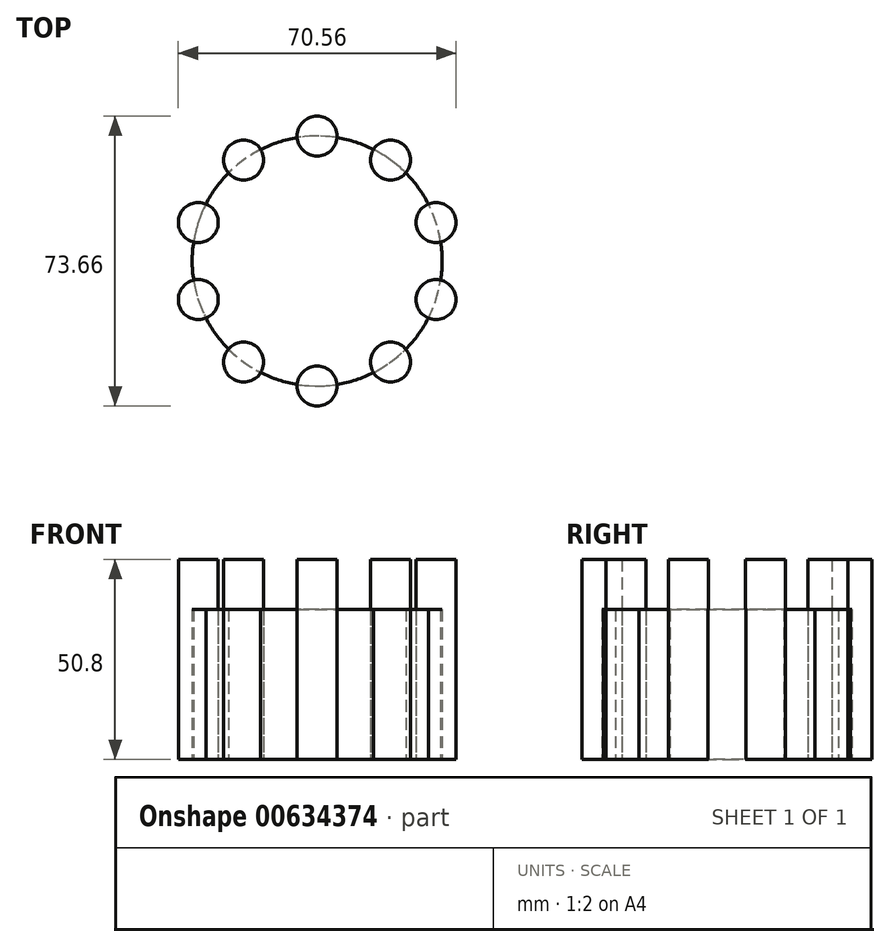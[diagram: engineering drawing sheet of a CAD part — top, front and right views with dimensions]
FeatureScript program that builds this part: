
annotation { "Feature Type Name" : "Feature", "Feature Type Description" : "" }
export const myFeature = defineFeature(function(context is Context, id is Id, definition is map)
    precondition{}
    {
        {
            var Q0;
            Q0=qCreatedBy(makeId("Top.planeOp"),FACE);
            var sketch = newSketch(context, id + "F0", { "sketchPlane" : qUnion([Q0])});
            skCircle(sketch, "E0", {"center": v(0, 0) * mm, "radius": 31.75 * mm});
            skSolve(sketch);
        }
        {
            var Q0;
            Q0=qSketchRegion(id+"F0",true);
            extrude(context, id + "F1", {"entities" : qUnion([Q0]), "depth" : 38.1 * mm});
        }
        {
            var Q0;
            Q0=qCreatedBy(makeId("Top.planeOp"),FACE);
            var sketch = newSketch(context, id + "F2", { "sketchPlane" : qUnion([Q0])});
            skCircle(sketch, "E1", {"center": v(0, 31.75) * mm, "radius": 5.08 * mm});
            skCircle(sketch, "E2.1.0", {"center": v(-18.66, 25.69) * mm, "radius": 5.08 * mm});
            skCircle(sketch, "E2.2.0", {"center": v(-30.2, 9.81) * mm, "radius": 5.08 * mm});
            skCircle(sketch, "E2.3.0", {"center": v(-30.2, -9.81) * mm, "radius": 5.08 * mm});
            skCircle(sketch, "E2.4.0", {"center": v(-18.66, -25.69) * mm, "radius": 5.08 * mm});
            skCircle(sketch, "E2.5.0", {"center": v(0, -31.75) * mm, "radius": 5.08 * mm});
            skCircle(sketch, "E2.6.0", {"center": v(18.66, -25.69) * mm, "radius": 5.08 * mm});
            skCircle(sketch, "E2.7.0", {"center": v(30.2, -9.81) * mm, "radius": 5.08 * mm});
            skCircle(sketch, "E2.8.0", {"center": v(30.2, 9.81) * mm, "radius": 5.08 * mm});
            skCircle(sketch, "E2.9.0", {"center": v(18.66, 25.69) * mm, "radius": 5.08 * mm});
            skPoint(sketch, "E2.center", {"position": v(0, 0) * mm});
            skSolve(sketch);
        }
        {
            var Q0;
            Q0=qSketchRegion(id+"F2",true);
            extrude(context, id + "F3", {"entities" : qUnion([Q0]), "depth" : 50.8 * mm});
        }
        {
            var Q0;
            Q0=makeQuery(id+"F1.opExtrude","SWEPT_BODY",BODY,{"disambiguationData":[OSD([sQuery(id+"F0.wireOp",EDGE,"E0")])]});
            var Q1;
            Q1=makeQuery(id+"F3.opExtrude","SWEPT_BODY",BODY,{"disambiguationData":[OSD([sQuery(id+"F2.wireOp",EDGE,"E1")])]});
            var Q2;
            Q2=makeQuery(id+"F3.opExtrude","SWEPT_BODY",BODY,{"disambiguationData":[OSD([sQuery(id+"F2.wireOp",EDGE,"E2.1.0")])]});
            var Q3;
            Q3=makeQuery(id+"F3.opExtrude","SWEPT_BODY",BODY,{"disambiguationData":[OSD([sQuery(id+"F2.wireOp",EDGE,"E2.2.0")])]});
            var Q4;
            Q4=makeQuery(id+"F3.opExtrude","SWEPT_BODY",BODY,{"disambiguationData":[OSD([sQuery(id+"F2.wireOp",EDGE,"E2.3.0")])]});
            var Q5;
            Q5=makeQuery(id+"F3.opExtrude","SWEPT_BODY",BODY,{"disambiguationData":[OSD([sQuery(id+"F2.wireOp",EDGE,"E2.4.0")])]});
            var Q6;
            Q6=makeQuery(id+"F3.opExtrude","SWEPT_BODY",BODY,{"disambiguationData":[OSD([sQuery(id+"F2.wireOp",EDGE,"E2.5.0")])]});
            var Q7;
            Q7=makeQuery(id+"F3.opExtrude","SWEPT_BODY",BODY,{"disambiguationData":[OSD([sQuery(id+"F2.wireOp",EDGE,"E2.6.0")])]});
            var Q8;
            Q8=makeQuery(id+"F3.opExtrude","SWEPT_BODY",BODY,{"disambiguationData":[OSD([sQuery(id+"F2.wireOp",EDGE,"E2.7.0")])]});
            var Q9;
            Q9=makeQuery(id+"F3.opExtrude","SWEPT_BODY",BODY,{"disambiguationData":[OSD([sQuery(id+"F2.wireOp",EDGE,"E2.8.0")])]});
            var Q10;
            Q10=makeQuery(id+"F3.opExtrude","SWEPT_BODY",BODY,{"disambiguationData":[OSD([sQuery(id+"F2.wireOp",EDGE,"E2.9.0")])]});
            booleanBodies(context, id + "F4", {"operationType" : BooleanOperationType.INTERSECTION, "tools" : qUnion([Q0, Q1, Q2, Q3, Q4, Q5, Q6, Q7, Q8, Q9, Q10]), "keepTools" : true});
        }
        {
            var Q0;
            Q0=makeQuery(id+"F3.opExtrude","SWEPT_BODY",BODY,{"disambiguationData":[OSD([sQuery(id+"F2.wireOp",EDGE,"E2.2.0")])]});
            var Q1;
            Q1=makeQuery(id+"F1.opExtrude","SWEPT_BODY",BODY,{"disambiguationData":[OSD([sQuery(id+"F0.wireOp",EDGE,"E0")])]});
            booleanBodies(context, id + "F5", {"operationType" : BooleanOperationType.INTERSECTION, "tools" : qUnion([Q0, Q1]), "keepTools" : true});
        }
        {
            var Q0;
            Q0=makeQuery(id+"F3.opExtrude","SWEPT_BODY",BODY,{"disambiguationData":[OSD([sQuery(id+"F2.wireOp",EDGE,"E2.3.0")])]});
            var Q1;
            Q1=makeQuery(id+"F1.opExtrude","SWEPT_BODY",BODY,{"disambiguationData":[OSD([sQuery(id+"F0.wireOp",EDGE,"E0")])]});
            booleanBodies(context, id + "F6", {"operationType" : BooleanOperationType.INTERSECTION, "tools" : qUnion([Q0, Q1]), "keepTools" : true});
        }
        {
            var Q0;
            Q0=makeQuery(id+"F3.opExtrude","SWEPT_BODY",BODY,{"disambiguationData":[OSD([sQuery(id+"F2.wireOp",EDGE,"E2.4.0")])]});
            var Q1;
            Q1=makeQuery(id+"F1.opExtrude","SWEPT_BODY",BODY,{"disambiguationData":[OSD([sQuery(id+"F0.wireOp",EDGE,"E0")])]});
            booleanBodies(context, id + "F7", {"operationType" : BooleanOperationType.INTERSECTION, "tools" : qUnion([Q0, Q1]), "keepTools" : true});
        }
        {
            var Q0;
            Q0=makeQuery(id+"F3.opExtrude","SWEPT_BODY",BODY,{"disambiguationData":[OSD([sQuery(id+"F2.wireOp",EDGE,"E2.5.0")])]});
            var Q1;
            Q1=makeQuery(id+"F1.opExtrude","SWEPT_BODY",BODY,{"disambiguationData":[OSD([sQuery(id+"F0.wireOp",EDGE,"E0")])]});
            booleanBodies(context, id + "F8", {"operationType" : BooleanOperationType.INTERSECTION, "tools" : qUnion([Q0, Q1]), "keepTools" : true});
        }
        {
            var Q0;
            Q0=makeQuery(id+"F3.opExtrude","SWEPT_BODY",BODY,{"disambiguationData":[OSD([sQuery(id+"F2.wireOp",EDGE,"E2.6.0")])]});
            var Q1;
            Q1=makeQuery(id+"F1.opExtrude","SWEPT_BODY",BODY,{"disambiguationData":[OSD([sQuery(id+"F0.wireOp",EDGE,"E0")])]});
            booleanBodies(context, id + "F9", {"operationType" : BooleanOperationType.INTERSECTION, "tools" : qUnion([Q0, Q1]), "keepTools" : true});
        }
        {
            var Q0;
            Q0=makeQuery(id+"F3.opExtrude","SWEPT_BODY",BODY,{"disambiguationData":[OSD([sQuery(id+"F2.wireOp",EDGE,"E2.7.0")])]});
            var Q1;
            Q1=makeQuery(id+"F1.opExtrude","SWEPT_BODY",BODY,{"disambiguationData":[OSD([sQuery(id+"F0.wireOp",EDGE,"E0")])]});
            booleanBodies(context, id + "F10", {"operationType" : BooleanOperationType.INTERSECTION, "tools" : qUnion([Q0, Q1]), "keepTools" : true});
        }
        {
            var Q0;
            Q0=makeQuery(id+"F3.opExtrude","SWEPT_BODY",BODY,{"disambiguationData":[OSD([sQuery(id+"F2.wireOp",EDGE,"E2.8.0")])]});
            var Q1;
            Q1=makeQuery(id+"F1.opExtrude","SWEPT_BODY",BODY,{"disambiguationData":[OSD([sQuery(id+"F0.wireOp",EDGE,"E0")])]});
            booleanBodies(context, id + "F11", {"operationType" : BooleanOperationType.INTERSECTION, "tools" : qUnion([Q0, Q1]), "keepTools" : true});
        }
        {
            var Q0;
            Q0=makeQuery(id+"F3.opExtrude","SWEPT_BODY",BODY,{"disambiguationData":[OSD([sQuery(id+"F2.wireOp",EDGE,"E2.9.0")])]});
            var Q1;
            Q1=makeQuery(id+"F1.opExtrude","SWEPT_BODY",BODY,{"disambiguationData":[OSD([sQuery(id+"F0.wireOp",EDGE,"E0")])]});
            booleanBodies(context, id + "F12", {"operationType" : BooleanOperationType.INTERSECTION, "tools" : qUnion([Q0, Q1]), "keepTools" : true});
        }
        {
            var Q0;
            Q0=makeQuery(id+"F3.opExtrude","SWEPT_BODY",BODY,{"disambiguationData":[OSD([sQuery(id+"F2.wireOp",EDGE,"E1")])]});
            var Q1;
            Q1=makeQuery(id+"F1.opExtrude","SWEPT_BODY",BODY,{"disambiguationData":[OSD([sQuery(id+"F0.wireOp",EDGE,"E0")])]});
            booleanBodies(context, id + "F13", {"operationType" : BooleanOperationType.INTERSECTION, "tools" : qUnion([Q0, Q1]), "keepTools" : true});
        }
        {
            var Q0;
            Q0=makeQuery(id+"F1.opExtrude","SWEPT_BODY",BODY,{"disambiguationData":[OSD([sQuery(id+"F0.wireOp",EDGE,"E0")])]});
            var Q1;
            Q1=makeQuery(id+"F3.opExtrude","SWEPT_BODY",BODY,{"disambiguationData":[OSD([sQuery(id+"F2.wireOp",EDGE,"E2.1.0")])]});
            booleanBodies(context, id + "F14", {"operationType" : BooleanOperationType.INTERSECTION, "tools" : qUnion([Q0, Q1]), "keepTools" : true});
        }
        {
            var Q0;
            Q0=makeQuery(id+"F3.opExtrude","SWEPT_BODY",BODY,{"disambiguationData":[OSD([sQuery(id+"F2.wireOp",EDGE,"E2.2.0")])]});
            var Q1;
            Q1=makeQuery(id+"F1.opExtrude","SWEPT_BODY",BODY,{"disambiguationData":[OSD([sQuery(id+"F0.wireOp",EDGE,"E0")])]});
            booleanBodies(context, id + "F15", {"operationType" : BooleanOperationType.INTERSECTION, "tools" : qUnion([Q0, Q1]), "keepTools" : true});
        }
    });
